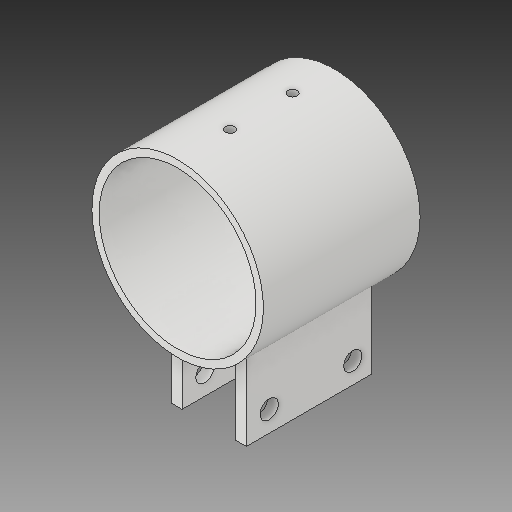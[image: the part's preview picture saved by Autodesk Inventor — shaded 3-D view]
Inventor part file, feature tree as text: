
AUTODESK INVENTOR PART (.ipt)
format: ipt  version: 2018.2 (Build 222227000, 227)  size: 161,280 bytes
history: native  units: mm
features: extrude x4, sketch x3
ambient origin geometry x8: Origin, YZ Plane, XZ Plane, XY Plane, X Axis, Y Axis, Z Axis, Center Point
bodies: Solid1 (feature_tree)
feature tree (7):
  sketch  "Sketch1"  dims[d0=1.4mm d1=30.0mm]
  extrude  "Extrusion1"  Depth=30.0mm
  extrude  "Extrusion3"  Depth=10.3mm
  extrude  "Extrusion2"  Depth=20.0mm TaperAngle=0.0deg
  extrude  "Extrusion4"  Depth=20.0mm
  sketch  "Sketch2"  dims[d2=2.0mm d3=10.3mm]
  sketch  "Sketch3"  dims[d4=15.0mm d5=30.0mm d6=0.0mm d7=3.5mm d8=3.5mm d9=16.0mm d11=20.0mm d12=0.0mm d13=24.0mm d14=0.0mm d15=4.0mm d16=1.8mm d18=12.0mm d19=8.0mm d20=20.0mm d21=0.0mm]
